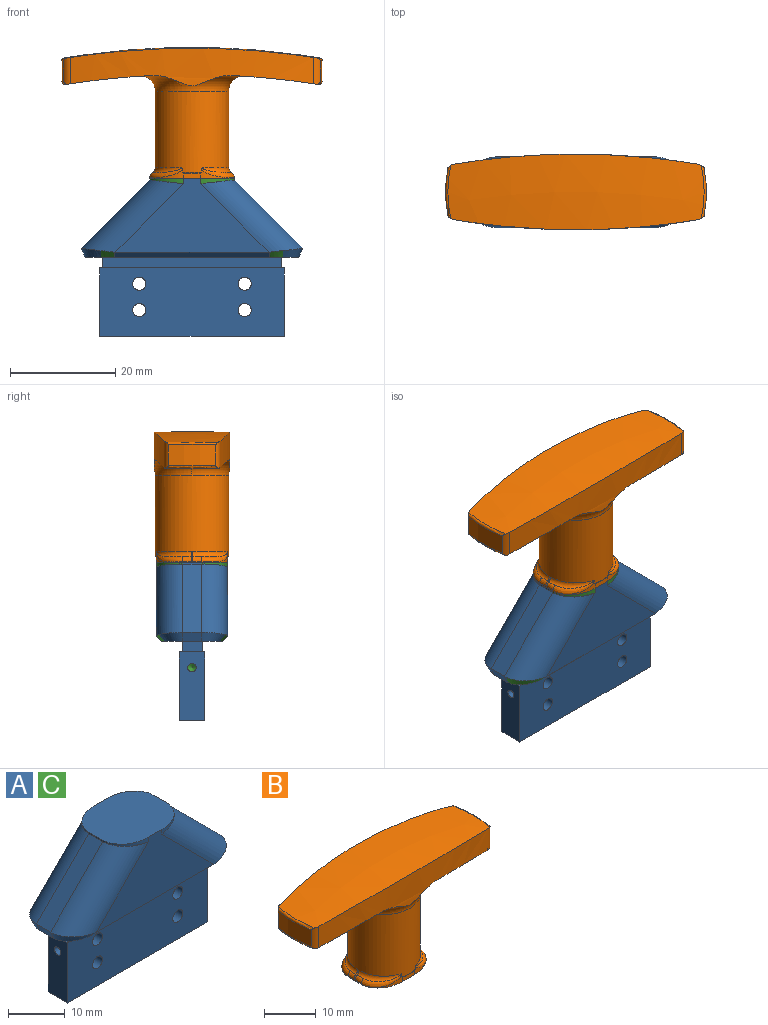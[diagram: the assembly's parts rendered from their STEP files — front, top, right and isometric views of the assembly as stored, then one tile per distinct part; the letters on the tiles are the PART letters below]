
ASSEMBLY  parts=3 mates=1
PART A: 48 faces, bbox 42x13.5x32.5 mm
  f0: cylinder r=5mm len=19.36mm, axis (0.71,0,-0.71), area 140.8mm2, adj f1,f43,f44,f45,f46,f47
  f1: plane 29.27x14mm, normal (0,1,0), area 214.8mm2, adj f0,f2,f38,f39,f42,f46
  f2: plane 29.27x1mm, normal (0,0.71,-0.71), area 41.4mm2, adj f1,f3,f21,f43
  f3: bspline ~6.36x5mm, area 14mm2, adj f2,f4,f21,f42
  f4: plane 3.5x1.71mm, normal (-0.92,0,-0.38), area 6.5mm2, adj f3,f5,f20,f21
  f5: plane 13x13mm, normal (-0.71,0,0.71), area 64.3mm2, adj f4,f6,f19,f42
  f6: plane 3.5x0.29mm, normal (-1,0,0), area 1mm2, adj f5,f7,f38,f39
  f7: extruded ~6.36x5mm, area 5.1mm2, adj f6,f8,f9,f18,f19,f38
  f8: bspline ~3.33x1.61mm, area 0mm2, adj f7,f19
  f9: plane 29.27x14mm, normal (0,-1,0), area 214.8mm2, adj f7,f10,f13,f17,f19,f38
  f10: plane 29.27x1mm, normal (0,-0.71,-0.71), area 41.4mm2, adj f9,f11,f20,f21
  f11: bspline ~6.36x5mm, area 14mm2, adj f10,f12,f17,f21
  f12: plane 3.5x1.71mm, normal (0.92,0,-0.38), area 6.5mm2, adj f11,f21,f43,f44
  f13: extruded ~6.37x5mm, area 5.1mm2, adj f9,f14,f15,f16,f17,f38
  f14: bspline ~3.13x0.65mm, area 0mm2, adj f13,f17
  f15: bspline ~2.62x1.56mm, area 0mm2, adj f13,f17
  f16: plane 3.5x0.29mm, normal (1,0,0), area 1mm2, adj f13,f38,f44,f46
  f17: cylinder r=5mm len=19.36mm, axis (0.71,0,-0.71), area 144.8mm2, adj f9,f11,f13,f14,f15,f44
  f18: bspline ~3.13x0.65mm, area 0mm2, adj f7,f19
  f19: cylinder r=5mm len=19.36mm, axis (0.71,0,0.71), area 140.8mm2, adj f5,f7,f8,f9,f18,f20
  f20: bspline ~6.36x5mm, area 14mm2, adj f4,f10,f19,f21
  f21: plane 40.58x11.5mm, normal (0,0,-1), area 318.1mm2, adj f2,f3,f4,f10,f11,f12,f20,f22
  f22: plane 34x2mm, normal (0,-1,0), area 68mm2, adj f21,f23,f35,f37
  f23: plane 35x4.8mm, normal (0,0,1), area 38.8mm2, adj f22,f24,f30,f33,f34,f35,f36,f37
  f24: plane 35x13mm, normal (0,-1,0), area 435.4mm2, adj f23,f25,f26,f27,f28,f29,f30,f34
  f25: cylinder r=1.25mm len=4.8mm, axis (0,1,0), area 37.7mm2, adj f24,f33
  f26: cylinder r=1.25mm len=4.8mm, axis (0,1,0), area 37.7mm2, adj f24,f33
  f27: cylinder r=1.25mm len=4.8mm, axis (0,1,0), area 37.7mm2, adj f24,f33
  f28: cylinder r=1.25mm len=4.8mm, axis (0,1,0), area 37.7mm2, adj f24,f33
  f29: plane 35x4.8mm, normal (0,0,-1), area 168mm2, adj f24,f30,f33,f34
  f30: plane 13x4.8mm, normal (-1,0,0), area 60.4mm2, adj f23,f24,f29,f31,f33
  f31: cylinder r=0.8mm len=5mm, axis (-1,0,0), area 25.1mm2, adj f30,f32
  f32: cone r=0.8mm half-angle=59deg, axis (-1,0,0), area 2.3mm2, adj f31
  f33: plane 35x13mm, normal (0,1,0), area 435.4mm2, adj f23,f25,f26,f27,f28,f29,f30,f34
  f34: plane 13x4.8mm, normal (1,0,0), area 62.4mm2, adj f23,f24,f29,f33
  f35: plane 3.8x2mm, normal (-1,0,0), area 7.6mm2, adj f21,f22,f23,f36
  f36: plane 34x2mm, normal (0,1,0), area 68mm2, adj f21,f23,f35,f37
  f37: plane 3.8x2mm, normal (1,0,0), area 7.6mm2, adj f21,f22,f23,f36
  f38: plane 16.03x13.5mm, normal (0,0,1), area 188.5mm2, adj f1,f6,f7,f9,f13,f16,f39,f46
  f39: extruded ~6.36x5mm, area 5.1mm2, adj f1,f6,f38,f40,f41,f42
  f40: bspline ~3.08x0.63mm, area 0mm2, adj f39,f42
  f41: bspline ~3.33x1.61mm, area 0mm2, adj f39,f42
  f42: cylinder r=5mm len=19.36mm, axis (0.71,0,0.71), area 140.8mm2, adj f1,f3,f5,f39,f40,f41
  f43: bspline ~6.36x5mm, area 14mm2, adj f0,f2,f12,f21
  f44: plane 13x13mm, normal (0.71,0,0.71), area 64.3mm2, adj f0,f12,f16,f17
  f45: bspline ~3.34x1.63mm, area 0mm2, adj f0,f46
  f46: extruded ~6.36x5mm, area 5.1mm2, adj f0,f1,f16,f38,f45,f47
  f47: bspline ~3.1x0.63mm, area 0mm2, adj f0,f46
PART B: 47 faces, bbox 53.6x33.1x25 mm
  f0: plane 1.65x0.05mm, normal (0,0,-1), area 0.1mm2, adj f25,f35
  f1: plane 1.65x0.05mm, normal (0,0,-1), area 0.1mm2, adj f21,f36
  f2: cylinder r=7mm len=15.36mm, axis (0,0,1), area 646.7mm2, adj f3,f4,f20,f22,f24,f26,f29,f30
  f3: torus R=10mm, axis (0,0,-1), area 90.9mm2, adj f2,f4,f10,f15,f18
  f4: torus R=10mm, axis (0,0,-1), area 90.9mm2, adj f2,f3,f5,f15,f18
  f5: cylinder r=141mm len=46.15mm, axis (0,0,1), area 183.6mm2, adj f4,f6,f13,f14,f15,f18
  f6: cylinder r=2mm len=5.08mm, axis (0,0,1), area 7mm2, adj f5,f7,f8,f13,f18,f19
  f7: torus R=24.25mm, axis (0,0,-1), area 6.8mm2, adj f6,f8,f9,f13
  f8: cylinder r=24.75mm len=9.08mm, axis (0,0,1), area 36.4mm2, adj f6,f7,f9,f19
  f9: cylinder r=2mm len=5.08mm, axis (0,0,1), area 7mm2, adj f7,f8,f10,f13,f18,f19
  f10: cylinder r=141mm len=46.15mm, axis (0,0,1), area 183.6mm2, adj f3,f9,f11,f13,f15,f18
  f11: cylinder r=2mm len=5.08mm, axis (0,0,1), area 7mm2, adj f10,f12,f13,f15,f16,f17
  f12: torus R=24.25mm, axis (0,0,-1), area 6.8mm2, adj f11,f13,f14,f17
  f13: sphere r=146mm, area 630.3mm2, adj f5,f6,f7,f9,f10,f11,f12,f14
  f14: cylinder r=2mm len=5.08mm, axis (0,0,1), area 7mm2, adj f5,f12,f13,f15,f16,f17
  f15: sphere r=146mm, area 180.7mm2, adj f3,f4,f5,f10,f11,f14,f16
  f16: torus R=24.25mm, axis (0,0,-1), area 8.5mm2, adj f11,f14,f15,f17
  f17: cylinder r=24.75mm len=9.08mm, axis (0,0,1), area 36.4mm2, adj f11,f12,f14,f16
  f18: sphere r=146mm, area 180.7mm2, adj f3,f4,f5,f6,f9,f10,f19
  f19: torus R=24.25mm, axis (0,0,-1), area 8.5mm2, adj f6,f8,f9,f18
  f20: extruded ~6.36x5mm, area 3.9mm2, adj f2,f21,f27,f28,f36,f45,f46
  f21: plane 3.31x1.1mm, normal (0,1,0), area 3.3mm2, adj f1,f20,f22,f28,f36
  f22: extruded ~6.37x5mm, area 3.9mm2, adj f2,f21,f23,f28,f36,f38
  f23: plane 3.5x0.27mm, normal (1,0,0), area 0.8mm2, adj f22,f24,f28,f38,f39,f40,f41
  f24: extruded ~6.36x5mm, area 3.8mm2, adj f2,f23,f25,f28,f35,f37,f39
  f25: plane 3.31x1.1mm, normal (0,-1,0), area 3.3mm2, adj f0,f24,f26,f28,f35
  f26: extruded ~6.36x5mm, area 3.9mm2, adj f2,f25,f27,f28,f35,f42,f43
  f27: plane 3.5x0.27mm, normal (-1,0,0), area 0.8mm2, adj f20,f26,f28,f43,f44,f46
  f28: plane 16.03x13.5mm, normal (0,0,-1), area 188.5mm2, adj f20,f21,f22,f23,f24,f25,f26,f27
  f29: torus R=8mm, axis (0,0,-1), area 8.7mm2, adj f2,f30,f45,f46
  f30: bspline ~1.64x1.05mm, area 0.3mm2, adj f2,f29,f31,f44
  f31: torus R=8mm, axis (0,0,-1), area 8.7mm2, adj f2,f30,f42,f43
  f32: torus R=8mm, axis (0,0,-1), area 8.7mm2, adj f2,f33,f37,f39
  f33: bspline ~1.64x1.05mm, area 0.3mm2, adj f2,f32,f34,f41
  f34: torus R=8mm, axis (0,0,-1), area 8.7mm2, adj f2,f33,f38,f40
  f35: torus R=6.8mm, axis (0,0,1), area 0.9mm2, adj f0,f2,f24,f25,f26
  f36: torus R=6.8mm, axis (0,0,1), area 0.9mm2, adj f1,f2,f20,f21,f22
  f37: bspline ~6.28x5.33mm, area 8.3mm2, adj f2,f24,f32,f39
  f38: bspline ~6.28x5.06mm, area 8.3mm2, adj f2,f22,f23,f34,f40
  f39: bspline ~2.68x1.03mm, area 1.8mm2, adj f23,f24,f32,f37,f41
  f40: bspline ~2.68x1.03mm, area 1.8mm2, adj f23,f34,f38,f41
  f41: bspline ~1.73x0.89mm, area 0.3mm2, adj f23,f33,f39,f40
  f42: bspline ~6.29x5.21mm, area 8.3mm2, adj f2,f26,f31,f43
  f43: bspline ~2.52x1.03mm, area 1.8mm2, adj f26,f27,f31,f42,f44
  f44: bspline ~1.73x0.89mm, area 0.3mm2, adj f27,f30,f43,f46
  f45: bspline ~6.28x5.19mm, area 8.3mm2, adj f2,f20,f29,f46
  f46: bspline ~2.52x1.03mm, area 1.8mm2, adj f20,f27,f29,f44,f45
PART C: same geometry as A
PLACE A t=(-22.43,-7.37,-6.63)mm
PLACE B rot(axis=(0,-1,0),0deg) t=(-22.43,-7.37,24.37)mm
PLACE C t=(-22.43,-7.37,-6.63)mm
MATE fastened B.f7 <-> A.f38  axis (0,0,-1) through (-22.43,-7.37,23.37)mm
